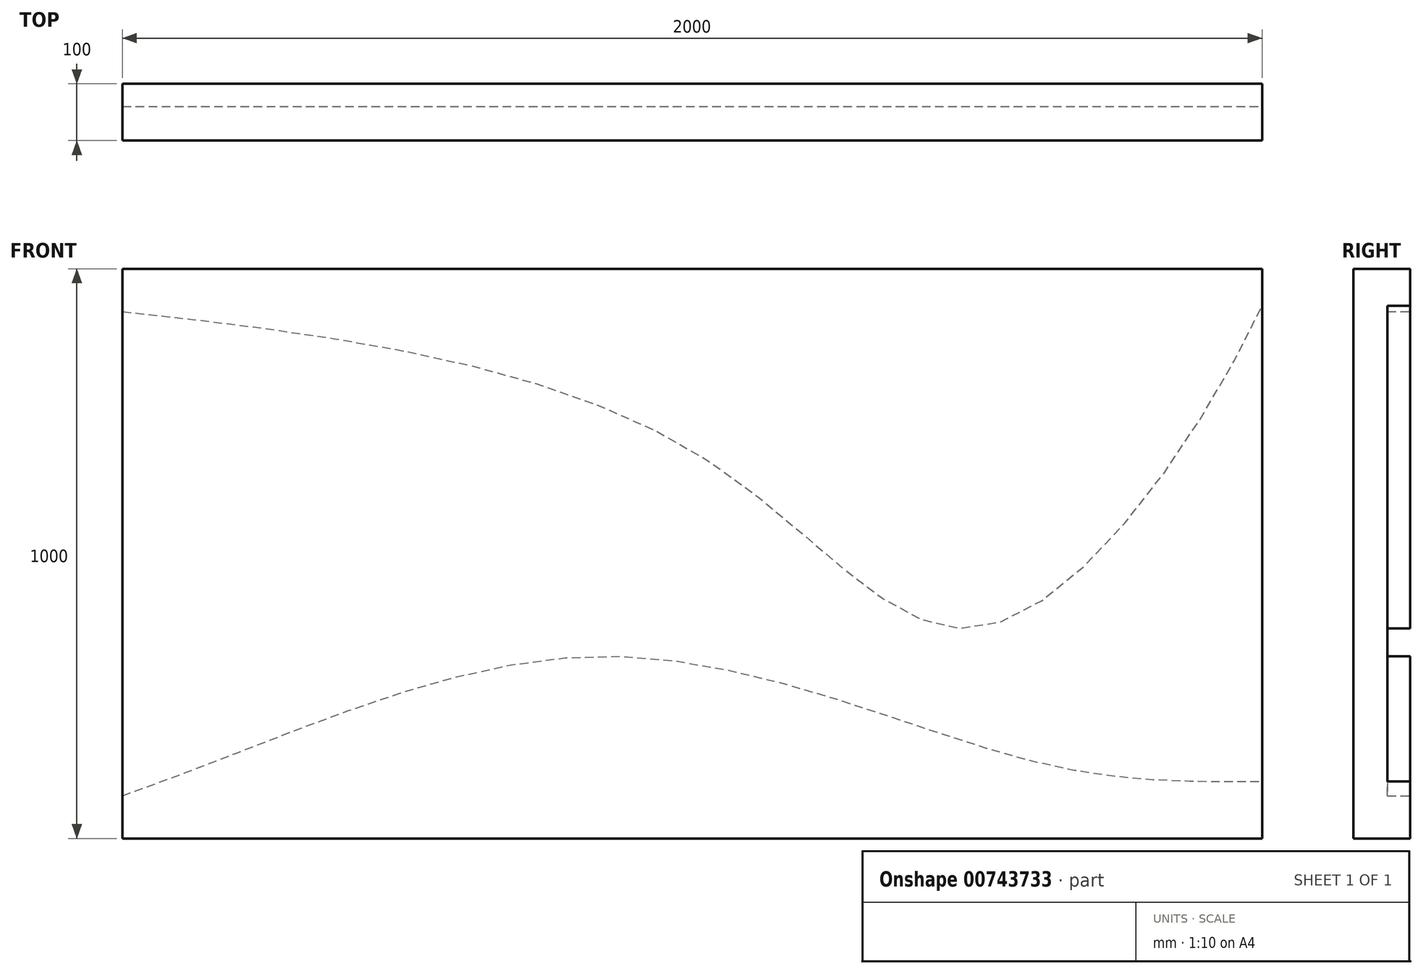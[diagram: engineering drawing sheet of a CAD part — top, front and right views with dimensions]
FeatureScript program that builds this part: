
annotation { "Feature Type Name" : "Feature", "Feature Type Description" : "" }
export const myFeature = defineFeature(function(context is Context, id is Id, definition is map)
    precondition{}
    {
        {
            var Q0;
            Q0=qCreatedBy(makeId("Front.planeOp"),FACE);
            var sketch = newSketch(context, id + "F0", { "sketchPlane" : qUnion([Q0])});
            skLineSegment(sketch, "E0.bottom", {"start": v(-1000, 500) * mm, "end": v(1000, 500) * mm});
            skLineSegment(sketch, "E0.top", {"start": v(-1000, -500) * mm, "end": v(1000, -500) * mm});
            skLineSegment(sketch, "E0.left", {"start": v(-1000, 500) * mm, "end": v(-1000, -500) * mm});
            skLineSegment(sketch, "E0.right", {"start": v(1000, 500) * mm, "end": v(1000, -500) * mm});
            skSolve(sketch);
        }
        {
            var Q0;
            Q0=makeQuery(id+"F0.imprint","IMPRINT",FACE,{"disambiguationData":[TD([[makeQuery(id+"F0.imprint","IMPRINT",EDGE,{"derivedFrom":sQuery(id+"F0.wireOp",EDGE,"E0.bottom")}),-1.0]])]});
            extrude(context, id + "F1", {"entities" : qUnion([Q0]), "depth" : 100 * mm, "offsetDistance" : 25 * mm});
        }
        {
            var Q0;
            Q0=makeQuery(id+"F0.imprint","IMPRINT",FACE,{"disambiguationData":[TD([[makeQuery(id+"F0.imprint","IMPRINT",EDGE,{"derivedFrom":sQuery(id+"F0.wireOp",EDGE,"E0.bottom")}),-1.0]])]});
            var sketch = newSketch(context, id + "F2", { "sketchPlane" : qUnion([Q0])});
            skFitSpline(sketch, "E1", {"points": [v(-1000, 425) * mm, v(25, 165) * mm, v(500, -130) * mm, v(1000, 435) * mm], "startDerivative": vector(2816.16, -308.62) * mm, "endDerivative": vector(1004.77, 2146.56) * mm});
            skFitSpline(sketch, "E2", {"points": [v(-1000, -425) * mm, v(-140, -180) * mm, v(600, -365) * mm, v(1000, -400) * mm], "startDerivative": vector(2334.31, 817) * mm, "endDerivative": vector(1451.48, 0) * mm});
            skLineSegment(sketch, "E3", {"start": v(-1000, 425) * mm, "end": v(-1000, -425) * mm});
            skLineSegment(sketch, "E4", {"start": v(1000, 435) * mm, "end": v(1000, -400) * mm});
            skSolve(sketch);
        }
        {
            var Q0;
            Q0=makeQuery(id+"F2.imprint","IMPRINT",FACE,{"disambiguationData":[TD([[makeQuery(id+"F2.imprint","IMPRINT",EDGE,{"derivedFrom":sQuery(id+"F2.wireOp",EDGE,"E1")}),-1.0]])]});
            extrude(context, id + "F3", {"entities" : qUnion([Q0]), "operationType" : NewBodyOperationType.REMOVE, "depth" : 40 * mm, "offsetDistance" : 25 * mm});
        }
    });
